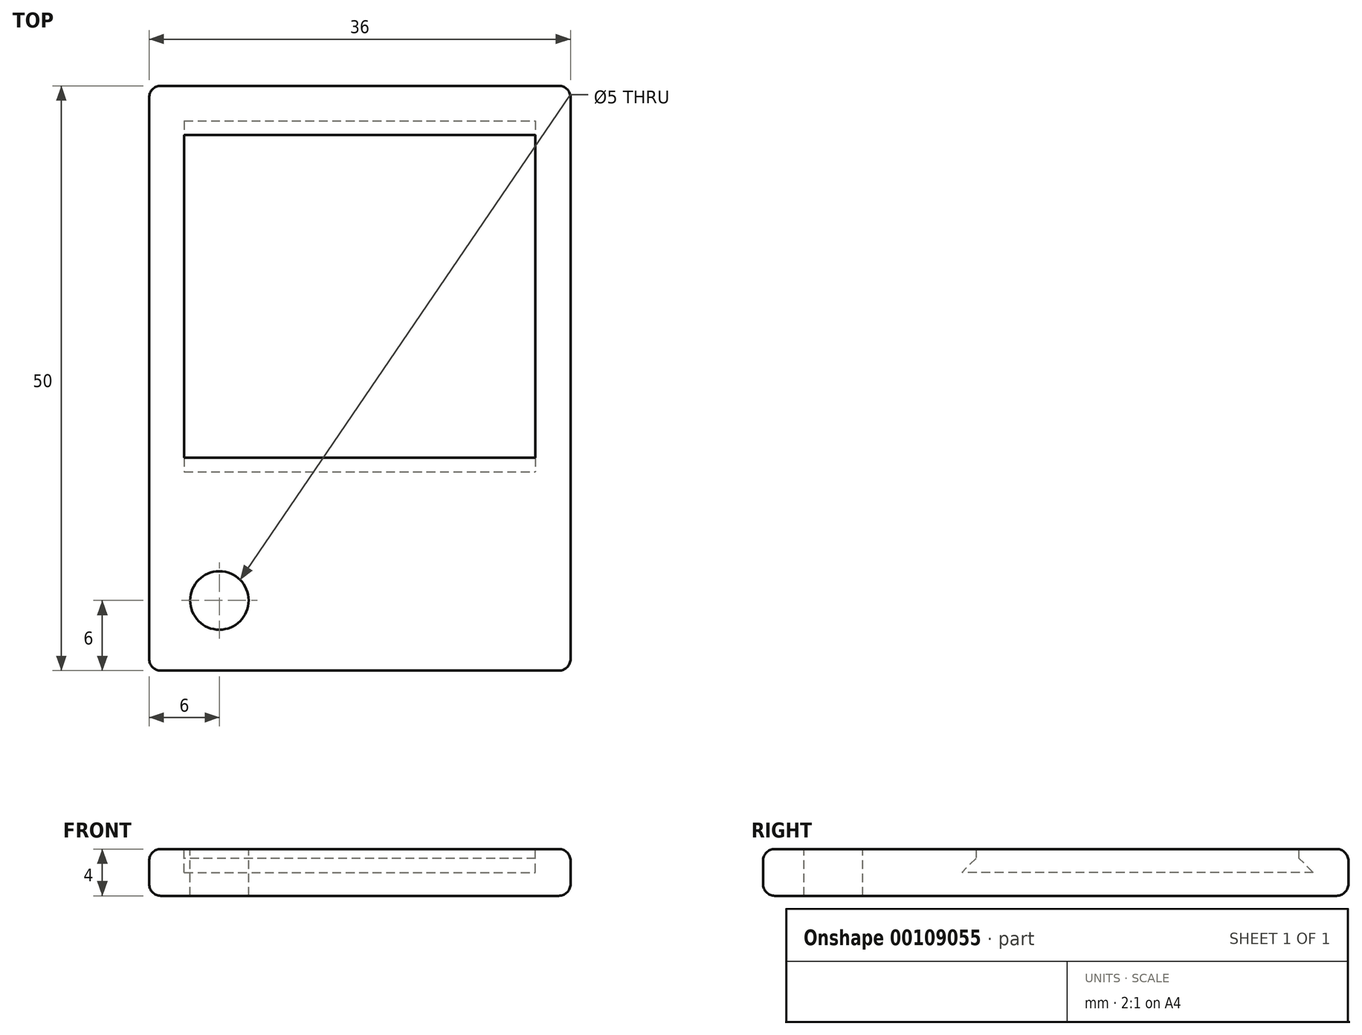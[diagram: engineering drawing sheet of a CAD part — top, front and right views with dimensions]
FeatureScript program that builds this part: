
annotation { "Feature Type Name" : "Feature", "Feature Type Description" : "" }
export const myFeature = defineFeature(function(context is Context, id is Id, definition is map)
    precondition{}
    {
        {
            var Q0;
            Q0=qCreatedBy(makeId("Top.planeOp"),FACE);
            var sketch = newSketch(context, id + "F0", { "sketchPlane" : qUnion([Q0])});
            skLineSegment(sketch, "E0.bottom", {"start": v(18, -25) * mm, "end": v(-18, -25) * mm});
            skLineSegment(sketch, "E0.top", {"start": v(18, 25) * mm, "end": v(-18, 25) * mm});
            skLineSegment(sketch, "E0.left", {"start": v(18, -25) * mm, "end": v(18, 25) * mm});
            skLineSegment(sketch, "E0.right", {"start": v(-18, -25) * mm, "end": v(-18, 25) * mm});
            skPoint(sketch, "E0.middle", {"position": v(0, 0) * mm});
            skSolve(sketch);
        }
        {
            var Q0;
            Q0 = qSketchRegion(id + "F0", true);
            extrude(context, id + "F1", {"entities" : qUnion([Q0]), "depth" : 4 * mm});
        }
        {
            var Q0;
            Q0=makeQuery(id+"F1.opExtrude","CAP_FACE",FACE,{"disambiguationData":[OSD([sQuery(id+"F0.wireOp",EDGE,"E0.bottom"),sQuery(id+"F0.wireOp",EDGE,"E0.top"),sQuery(id+"F0.wireOp",EDGE,"E0.left"),sQuery(id+"F0.wireOp",EDGE,"E0.right")])],"isStart":false});
            var sketch = newSketch(context, id + "F2", { "sketchPlane" : qUnion([Q0])});
            skLineSegment(sketch, "E1.bottom", {"start": v(-15, 22) * mm, "end": v(15, 22) * mm});
            skLineSegment(sketch, "E1.top", {"start": v(-15, -8) * mm, "end": v(15, -8) * mm});
            skLineSegment(sketch, "E1.left", {"start": v(-15, 22) * mm, "end": v(-15, -8) * mm});
            skLineSegment(sketch, "E1.right", {"start": v(15, 22) * mm, "end": v(15, -8) * mm});
            skSolve(sketch);
        }
        {
            var Q0;
            Q0=makeQuery(id+"F2.imprint","IMPRINT",FACE,{"disambiguationData":[TD([[makeQuery(id+"F2.imprint","IMPRINT",EDGE,{"derivedFrom":sQuery(id+"F2.wireOp",EDGE,"E1.bottom")}),-1.0]])]});
            extrude(context, id + "F3", {"entities" : qUnion([Q0]), "operationType" : NewBodyOperationType.REMOVE, "oppositeDirection" : true, "depth" : 2 * mm});
        }
        {
            var Q0;
            Q0=makeQuery(id+"F1.opExtrude","CAP_EDGE",EDGE,{"disambiguationData":[OSD([sQuery(id+"F0.wireOp",EDGE,"E0.bottom")])],"isStart":false});
            var Q1;
            Q1=makeQuery(id+"F1.opExtrude","CAP_EDGE",EDGE,{"disambiguationData":[OSD([sQuery(id+"F0.wireOp",EDGE,"E0.left")])],"isStart":false});
            var Q2;
            Q2=makeQuery(id+"F1.opExtrude","CAP_EDGE",EDGE,{"disambiguationData":[OSD([sQuery(id+"F0.wireOp",EDGE,"E0.top")])],"isStart":false});
            var Q3;
            Q3=makeQuery(id+"F1.opExtrude","CAP_EDGE",EDGE,{"disambiguationData":[OSD([sQuery(id+"F0.wireOp",EDGE,"E0.right")])],"isStart":false});
            var Q4;
            Q4=makeQuery(id+"F1.opExtrude","SWEPT_EDGE",EDGE,{"disambiguationData":[OSD([sQuery(id+"F0.wireOp",EDGE,"E0.bottom"),sQuery(id+"F0.wireOp",EDGE,"E0.left")])]});
            var Q5;
            Q5=makeQuery(id+"F1.opExtrude","SWEPT_EDGE",EDGE,{"disambiguationData":[OSD([sQuery(id+"F0.wireOp",EDGE,"E0.bottom"),sQuery(id+"F0.wireOp",EDGE,"E0.right")])]});
            var Q6;
            Q6=makeQuery(id+"F1.opExtrude","SWEPT_EDGE",EDGE,{"disambiguationData":[OSD([sQuery(id+"F0.wireOp",EDGE,"E0.top"),sQuery(id+"F0.wireOp",EDGE,"E0.left")])]});
            var Q7;
            Q7=makeQuery(id+"F1.opExtrude","CAP_EDGE",EDGE,{"disambiguationData":[OSD([sQuery(id+"F0.wireOp",EDGE,"E0.left")])],"isStart":true});
            var Q8;
            Q8=makeQuery(id+"F1.opExtrude","CAP_EDGE",EDGE,{"disambiguationData":[OSD([sQuery(id+"F0.wireOp",EDGE,"E0.bottom")])],"isStart":true});
            var Q9;
            Q9=makeQuery(id+"F1.opExtrude","CAP_EDGE",EDGE,{"disambiguationData":[OSD([sQuery(id+"F0.wireOp",EDGE,"E0.right")])],"isStart":true});
            var Q10;
            Q10=makeQuery(id+"F1.opExtrude","CAP_EDGE",EDGE,{"disambiguationData":[OSD([sQuery(id+"F0.wireOp",EDGE,"E0.top")])],"isStart":true});
            var Q11;
            Q11=makeQuery(id+"F1.opExtrude","SWEPT_EDGE",EDGE,{"disambiguationData":[OSD([sQuery(id+"F0.wireOp",EDGE,"E0.top"),sQuery(id+"F0.wireOp",EDGE,"E0.right")])]});
            fillet(context, id + "F4", {"entities" : qUnion([Q0, Q1, Q2, Q3, Q4, Q5, Q6, Q7, Q8, Q9, Q10, Q11]), "radius" : 1 * mm, "tangentPropagation" : true, "allowEdgeOverflow" : false});
        }
        {
            var Q0;
            Q0=qCreatedBy(makeId("Right.planeOp"),FACE);
            var sketch = newSketch(context, id + "F5", { "sketchPlane" : qUnion([Q0])});
            skLineSegment(sketch, "E2.0.1", {"start": v(-8, 4) * mm, "end": v(-8, 2) * mm});
            skLineSegment(sketch, "E2.0.3", {"start": v(-8, 2) * mm, "end": v(-8, 4) * mm});
            skLineSegment(sketch, "E3", {"start": v(-8, 2) * mm, "end": v(-8, 2) * mm});
            skLineSegment(sketch, "E4", {"start": v(-8, 4) * mm, "end": v(-8, 4) * mm});
            skLineSegment(sketch, "E5", {"start": v(-8, 2) * mm, "end": v(-6.8, 3.2) * mm});
            skLineSegment(sketch, "E6", {"start": v(-6.8, 3.2) * mm, "end": v(-6.8, 4) * mm});
            skLineSegment(sketch, "E7", {"start": v(-6.8, 4) * mm, "end": v(-8, 4) * mm});
            skSolve(sketch);
        }
        {
            var Q0;
            Q0 = qSketchRegion(id + "F5", true);
            extrude(context, id + "F6", {"entities" : qUnion([Q0]), "operationType" : NewBodyOperationType.ADD, "endBound" : BoundingType.UP_TO_NEXT, "depth" : 25 * mm, "hasSecondDirection" : true, "secondDirectionBound" : SecondDirectionBoundingType.UP_TO_NEXT, "secondDirectionOppositeDirection" : true, "secondDirectionDepth" : 25 * mm});
        }
        {
            var Q0;
            Q0=qCreatedBy(makeId("Right.planeOp"),FACE);
            var sketch = newSketch(context, id + "F7", { "sketchPlane" : qUnion([Q0])});
            skLineSegment(sketch, "E8.0.1", {"start": v(22, 4) * mm, "end": v(22, 2) * mm});
            skLineSegment(sketch, "E8.0.3", {"start": v(22, 2) * mm, "end": v(22, 4) * mm});
            skLineSegment(sketch, "E9", {"start": v(22, 4) * mm, "end": v(20.8, 4) * mm});
            skLineSegment(sketch, "E10", {"start": v(20.8, 4) * mm, "end": v(20.8, 3.2) * mm});
            skLineSegment(sketch, "E11", {"start": v(20.8, 3.2) * mm, "end": v(22, 2) * mm});
            skSolve(sketch);
        }
        {
            var Q0;
            Q0 = qSketchRegion(id + "F7", true);
            extrude(context, id + "F8", {"entities" : qUnion([Q0]), "operationType" : NewBodyOperationType.ADD, "endBound" : BoundingType.UP_TO_NEXT, "depth" : 25 * mm, "hasSecondDirection" : true, "secondDirectionBound" : SecondDirectionBoundingType.UP_TO_NEXT, "secondDirectionOppositeDirection" : true, "secondDirectionDepth" : 25 * mm});
        }
        {
            var Q0;
            Q0=makeQuery(id+"F8.boolean.opBoolean","MERGE",FACE,{"derivedFrom":[makeQuery(id+"F6.boolean.opBoolean","MERGE",FACE,{"derivedFrom":[makeQuery(id+"F1.opExtrude","CAP_FACE",FACE,{"disambiguationData":[OSD([sQuery(id+"F0.wireOp",EDGE,"E0.bottom"),sQuery(id+"F0.wireOp",EDGE,"E0.top"),sQuery(id+"F0.wireOp",EDGE,"E0.left"),sQuery(id+"F0.wireOp",EDGE,"E0.right")])],"isStart":false}),makeQuery(id+"F6.opExtrude","SWEPT_FACE",FACE,{"disambiguationData":[OSD([sQuery(id+"F5.wireOp",EDGE,"YZdoWrAD-sQyp-mvW0-mhO4-NZztvt0gITNn")])]})]}),makeQuery(id+"F8.opExtrude","SWEPT_FACE",FACE,{"disambiguationData":[OSD([sQuery(id+"F7.wireOp",EDGE,"Mb2jXTxl-iOQN-gCLb-rPTa-XlNAzhvbHKuY")])]})]});
            var sketch = newSketch(context, id + "F9", { "sketchPlane" : qUnion([Q0])});
            skCircle(sketch, "E12", {"center": v(-12, -19) * mm, "radius": 2.5 * mm});
            skSolve(sketch);
        }
        {
            var Q0;
            Q0 = qSketchRegion(id + "F9", true);
            extrude(context, id + "F10", {"entities" : qUnion([Q0]), "operationType" : NewBodyOperationType.REMOVE, "endBound" : BoundingType.THROUGH_ALL, "oppositeDirection" : true, "depth" : 25 * mm});
        }
    });
